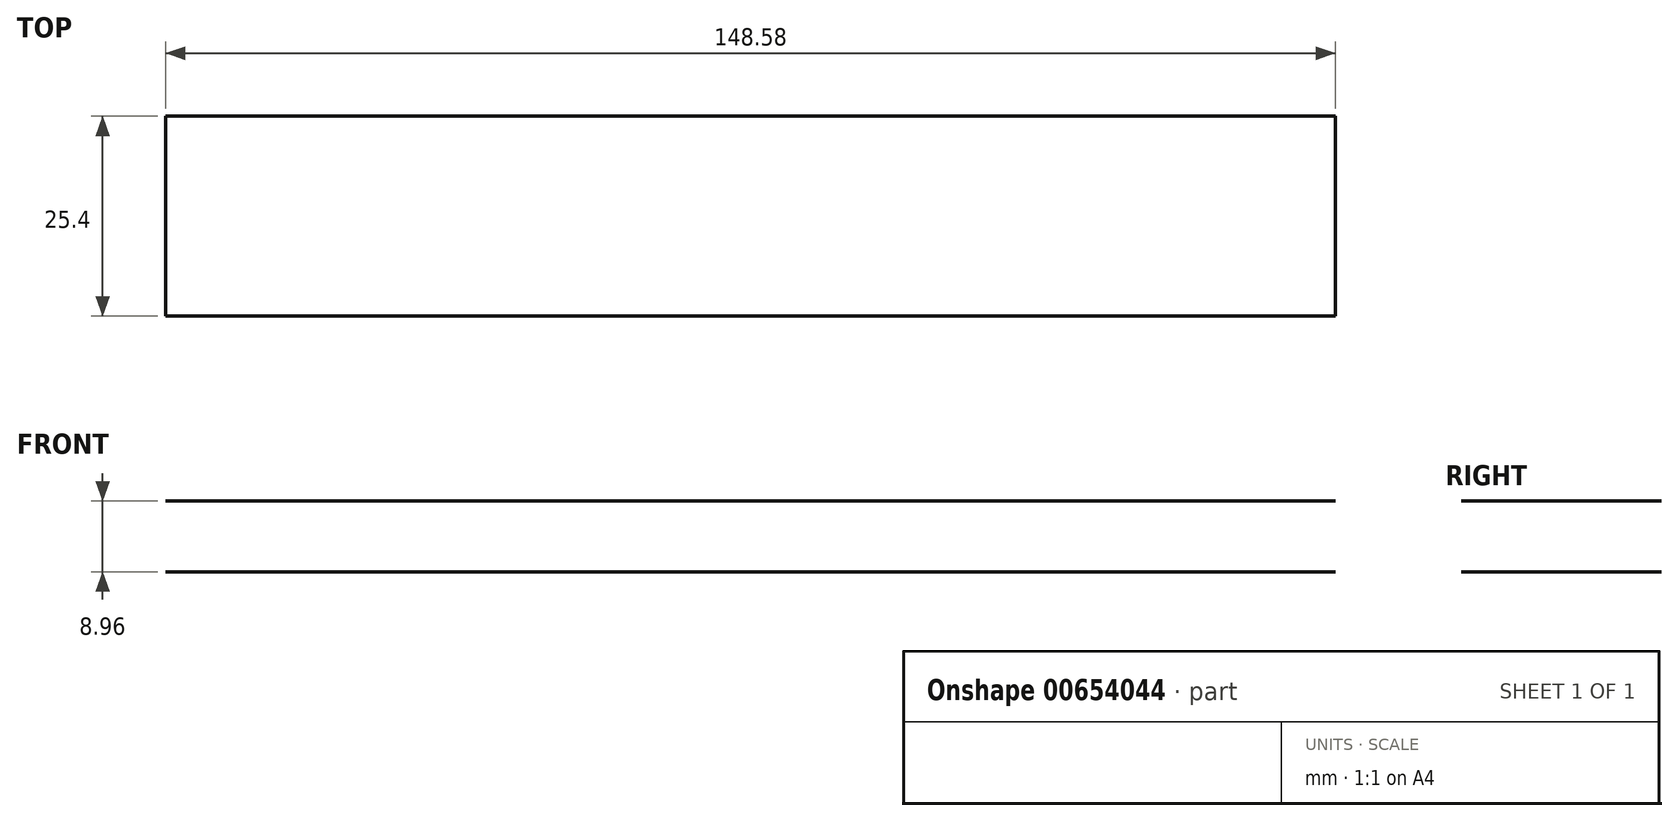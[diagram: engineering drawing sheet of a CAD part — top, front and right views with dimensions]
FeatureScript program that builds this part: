
annotation { "Feature Type Name" : "Feature", "Feature Type Description" : "" }
export const myFeature = defineFeature(function(context is Context, id is Id, definition is map)
    precondition{}
    {
        {
            var Q0;
            Q0=qCreatedBy(makeId("Front.planeOp"),FACE);
            var sketch = newSketch(context, id + "F0", { "sketchPlane" : qUnion([Q0])});
            skLineSegment(sketch, "E0.bottom", {"start": v(-74.85, 74.85) * mm, "end": v(73.73, 74.85) * mm});
            skLineSegment(sketch, "E0.top", {"start": v(-74.85, 65.89) * mm, "end": v(73.73, 65.89) * mm});
            skLineSegment(sketch, "E0.left", {"start": v(-74.85, 74.85) * mm, "end": v(-74.85, 65.89) * mm});
            skLineSegment(sketch, "E0.right", {"start": v(73.73, 74.85) * mm, "end": v(73.73, 65.89) * mm});
            skLineSegment(sketch, "E1.bottom", {"start": v(-74.85, 45.36) * mm, "end": v(74.1, 45.36) * mm});
            skLineSegment(sketch, "E1.top", {"start": v(-74.85, 35.65) * mm, "end": v(74.1, 35.65) * mm});
            skLineSegment(sketch, "E1.left", {"start": v(-74.85, 45.36) * mm, "end": v(-74.85, 35.65) * mm});
            skLineSegment(sketch, "E1.right", {"start": v(74.1, 45.36) * mm, "end": v(74.1, 35.65) * mm});
            skSolve(sketch);
        }
        {
            var Q0;
            Q0=sQuery(id+"F0.wireOp",EDGE,"E0.top");
            var Q1;
            Q1=sQuery(id+"F0.wireOp",EDGE,"E0.bottom");
            extrude(context, id + "F1", {"bodyType" : ToolBodyType.SURFACE, "surfaceEntities" : qUnion([Q0, Q1]), "depth" : 25.4 * mm, "offsetDistance" : 25.4 * mm});
        }
    });
